# Revit family: Blucher_PlumbingFixture_664Square_TwoPartDrain1
name_source: partatom
category: Plumbing Fixtures
revit_build: Autodesk Revit 2017 (Build: 20190508_0315(x64)
units: mm (PartAtom-declared; Revit-internal decimal feet)

## family parameters
Cut with Voids When Loaded = No
Host = Face
OmniClass Number = 23.70.50.21.24
OmniClass Title = Waste Water Drains
Part Type = Normal
Room Calculation Point = No
Round Connector Dimension = Use Diameter
Shared = No

## types (2) — shared parameters
Assembly Code = D2030300
AssetType = Fixed
BIMObjectName = Blucher_PlumbingFixture_664Square_TwoPartDrain
CW Connection = No
ClassificationName = Uniclass2015
ClassificationValue = Pr_65_52_24_24
Color = Stainless Steel
D = 160 mm  [stored 0.524934 ft]
Description = Kitchen Drain - Floor: Tile - Resin - Concrete
DocumentationCertificates = https://www.bimstore.co
DocumentationInstallationGuide = https://www.bimstore.co
DocumentationInstallationVideo = http://www.blucher.com
DocumentationLiterature = https://www.bimstore.co
DocumentationMaintenance = https://www.bimstore.co
DocumentationTechnical = https://www.bimstore.co
DurationUnit = Years
ExpectedLife = 50
FilterBasket_780.002.000.00 = FB : 780.002.000.00
FilterBasket_780.002.000.05 = FB : 780.002.000.05
Finish = 2B - Pickled
Grade = AISI 304/EN 1.4301 or AISI 316L/EN 1.4404
Grating_790.10 = G : 790.10 Plate
Grating_790.22 = G : 790.22 - Mesh
Grating_790.60 = G : 790.60 - Hygienic Pro
HW Connection = No
IfcExportAs = IfcFlowTerminal
IfcExportType = IfcWasteTerminalTypeEnum.FLOORWASTE
Keynote = R10
LowerPart_760.002.075 = LP_V_760.002 : 075
LowerPart_760.002.110 = LP_V_760.002 : 110
LowerPart_760.160.110 = LP_V_760.160 : 110
LowerPart_763.002.110 = LP_H_763.002.110 : 110
LowerPart_763.042.110 = LP_H_763.042.110 : 110
LowerPart_769.002.110 = LP_H_769.002.110 : 110
LowerPart_771.002.110 = LP_H_771.002.110 : 110
LowerPart_774.002.075 = LP_V_774.002 : 075
LowerPart_774.002.110 = LP_V_774.002 : 110
LowerPart_775.002.075 = LP_V_775.002 : 075
LowerPart_775.002.110 = LP_V_775.002 : 110
Manufacturer = BLÜCHER
ManufacturerName = BLÜCHER
Material = Available in Stainless Steel AISI 304 & Stainless Steel AISI 316L
Model = BLÜCHER Kitchen Drain 664 Square
ModelReference = BLÜCHER Kitchen Drain 664 Square
NBSDescription = Drainage channels with gratings
NBSObjectName = BLÜCHER - Drainage channels with gratings
NBSReference = 90-05-20/422
ProductionYear = 2019
ReferencedStandard = EN1253
Shape = Square
Type Comments = Kitchen Drain 664 Square
TypeName = Kitchen Drain 664 Square
URL = http://www.blucher.com
UpperPartType_774.402.000 = SC : 774.402.000
Vent Connection = No
WarrantyDurationUnit = Years
Waste Connection = Yes
WaterTrap_562.102.000 = WT : 562.102.000
_BSBibleVersion = 15
_CurrentRevision = 1
_DistributedBy = www.bimstore.co.uk
zero-valued in all types: Default Elevation, HeightFromLevel, _BimSpecGuid

## per-type parameters (varying)
| type | ChannelProductCode | ChannelType | F | F1 | GratingWidth | H | H1 | H5 | NominalDepth | NominalLength | Size |
| Square - 300mm(W) x 300mm(L) x 161mm(H) | 710.423.000 | SC : 710.403.000 | 300 mm | 300 mm | 268 mm  [stored 0.879265 ft] | 161 mm  [stored 0.528215 ft] | 91 mm | 70 mm  [stored 0.229659 ft] | 300 mm | 300 mm | 300mm(W) x 300mm(L) x 161mm(H) |
| Square - 200mm(W) x 200mm(L) x 147mm(H) | 774.422.000 | SC : 774.402.000 | 200 mm  [stored 0.656168 ft] | 200 mm  [stored 0.656168 ft] | 168 mm  [stored 0.551181 ft] | 147 mm  [stored 0.482283 ft] | 119 mm | 28 mm  [stored 0.0918635 ft] | 200 mm  [stored 0.656168 ft] | 200 mm  [stored 0.656168 ft] | 200mm(W) x 200mm(L) x 147mm(H) |

note: [stored X ft] marks values corroborated as IEEE doubles in the binary element streams (Revit-internal decimal feet)

## geometry (parser evidence)
native form markers: Sweep x33
no freeform markers — native parametric forms only
